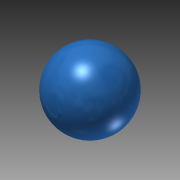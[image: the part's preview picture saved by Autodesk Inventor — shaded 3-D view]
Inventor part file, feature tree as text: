
AUTODESK INVENTOR PART (.ipt)
format: ipt  version: 2014 SP1 (Build 180222100, 222)  size: 104,448 bytes
history: native  units: in
note: dims shown in document units (in); Inventor stores cm internally (conversion verified against a paired STEP export)
features: revolve x1, sketch x1
ambient origin geometry x8: Origin, YZ Plane, XZ Plane, XY Plane, X Axis, Y Axis, Z Axis, Center Point
bodies: Solid1 (feature_tree)
feature tree (2):
  revolve  "Revolution1"  Angle=90.0deg
  sketch  "Sketch1"  dims[d0=25.0in d1=90.0deg]
